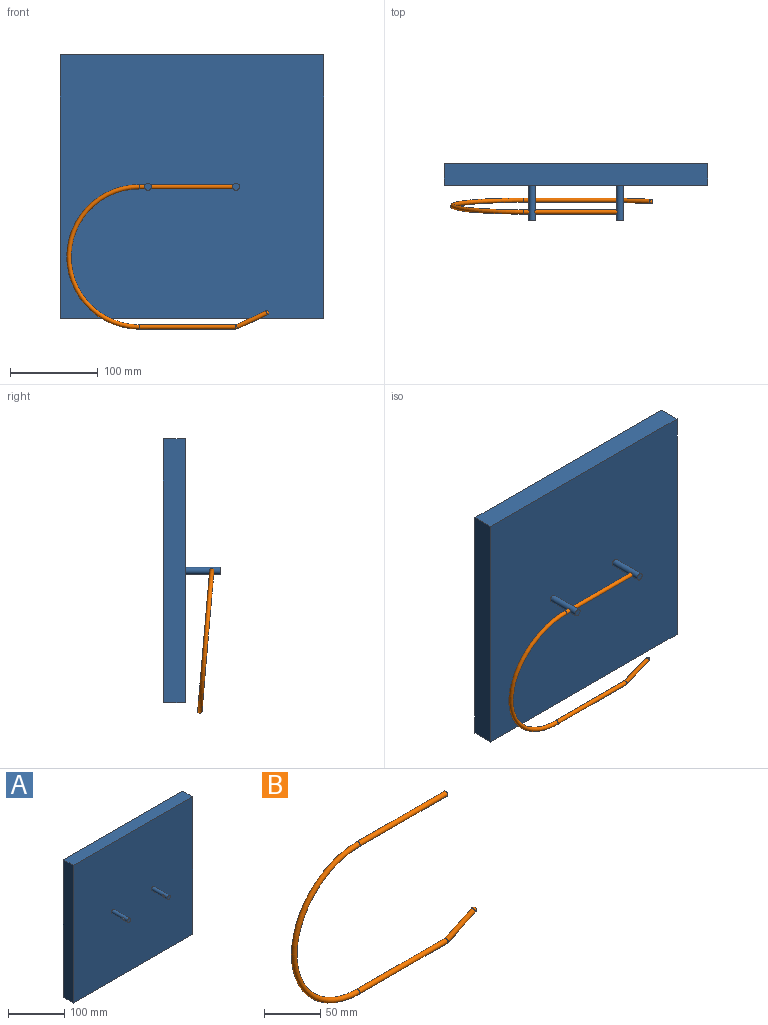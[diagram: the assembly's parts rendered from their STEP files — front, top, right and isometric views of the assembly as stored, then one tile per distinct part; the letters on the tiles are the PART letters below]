
ASSEMBLY  parts=2 mates=1
PART A: 13 faces, bbox 300x65x300 mm
  f0: plane 300x25mm, normal (0,0,1), area 7500mm2, adj f1,f3,f4,f5
  f1: plane 300x25mm, normal (-1,0,0), area 7500mm2, adj f0,f2,f4,f5
  f2: plane 300x25mm, normal (0,0,-1), area 7500mm2, adj f1,f3,f4,f5
  f3: plane 300x25mm, normal (1,0,0), area 7500mm2, adj f0,f2,f4,f5
  f4: plane 300x300mm, normal (0,-1,0), area 89899.5mm2, adj f0,f1,f2,f3,f6,f8
  f5: plane 300x300mm, normal (0,1,0), area 90000mm2, adj f0,f1,f2,f3
  f6: cylinder r=4mm len=40mm, axis (0,1,0), area 963.8mm2, adj f4,f7,f12
  f7: plane 8x8mm, normal (0,-1,0), area 50.3mm2, adj f6
  f8: cylinder r=4mm len=40mm, axis (0,1,0), area 984.5mm2, adj f4,f9,f11
  f9: plane 8x8mm, normal (0,-1,0), area 50.3mm2, adj f8
  f10: plane 5x5mm, normal (-1,0,0), area 19.6mm2, adj f11
  f11: cylinder r=2.5mm len=5mm, axis (1,0,0), area 56.2mm2, adj f8,f10
  f12: cylinder r=2.5mm len=8mm, axis (1,0,0), area 112.3mm2, adj f6
PART B: 7 faces, bbox 236.8x5x178.6 mm
  f0: plane 5x5mm, normal (1,0,0), area 19.6mm2, adj f1
  f1: cylinder r=2.5mm len=110mm, axis (-1,0,0), area 1727.9mm2, adj f0,f2
  f2: torus R=80mm, axis (0,-1,0), area 3947.8mm2, adj f1,f3
  f3: cylinder r=2.5mm len=110mm, axis (-1,0,0), area 1727.9mm2, adj f2,f4
  f4: torus R=2.5mm, axis (0,-1,0), area 17.1mm2, adj f3,f5
  f5: cylinder r=2.5mm len=36.1mm, axis (-0.91,0,-0.42), area 589mm2, adj f4,f6
  f6: sphere r=2.5mm, area 39.3mm2, adj f5
PLACE A t=(44.3,6.7,71.15)mm fixed
PLACE B rot(axis=(1,0,0),4.9deg) t=(39.3,-48.3,71.15)mm
MATE revolute B.f1 <-> A.f11  axis (-1,0,0) through (94.3,-48.3,71.15)mm
